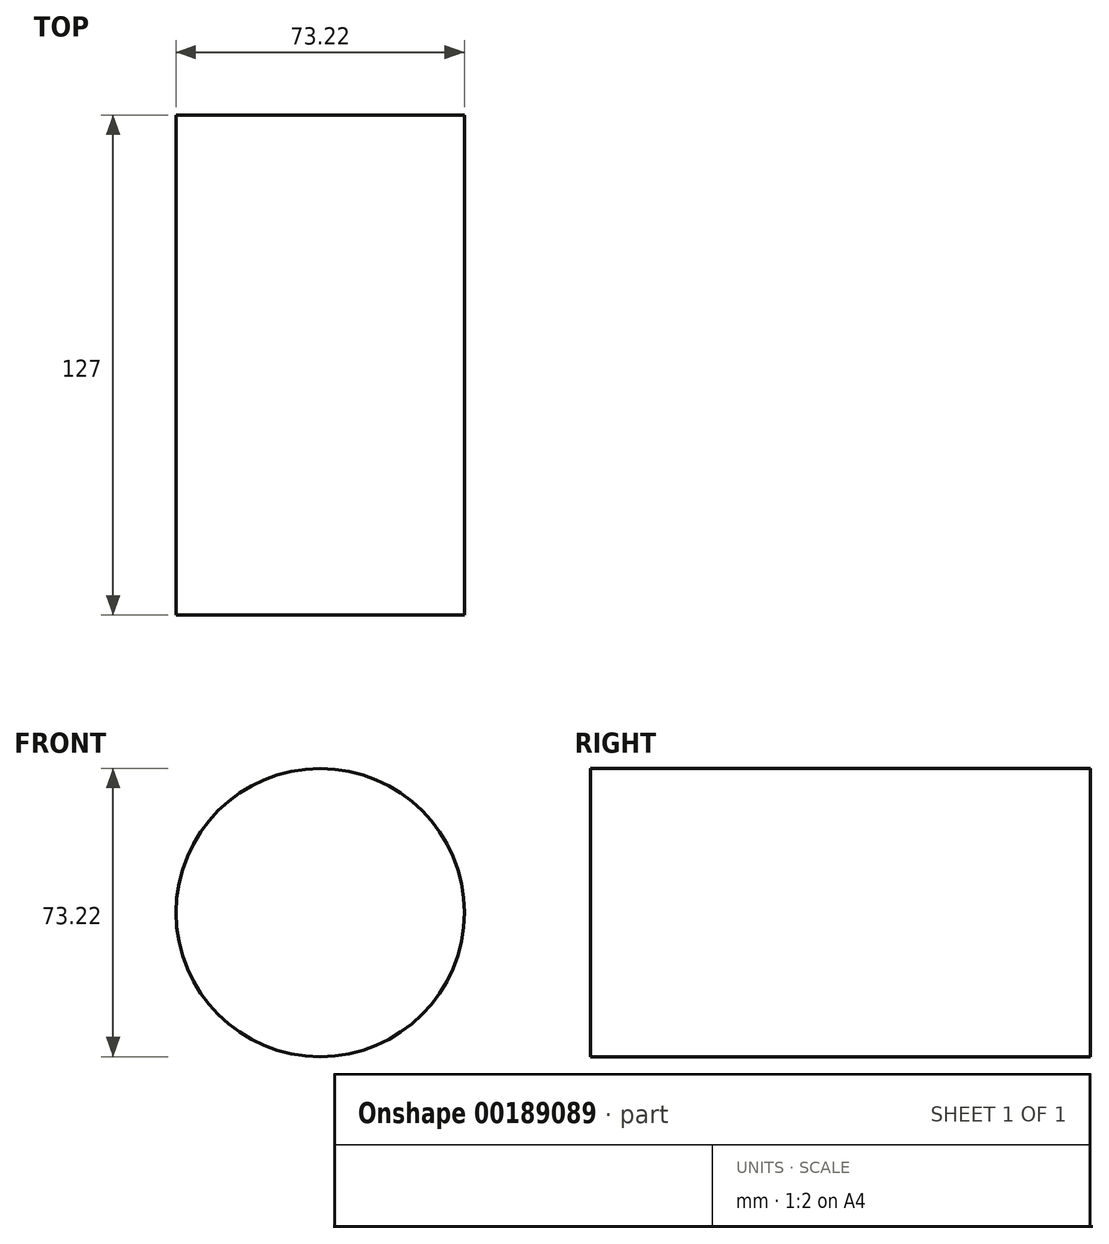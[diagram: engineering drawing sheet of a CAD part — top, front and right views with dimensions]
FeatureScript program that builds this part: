
annotation { "Feature Type Name" : "Feature", "Feature Type Description" : "" }
export const myFeature = defineFeature(function(context is Context, id is Id, definition is map)
    precondition{}
    {
        {
            var Q0;
            Q0=qCreatedBy(makeId("Front.planeOp"),FACE);
            var sketch = newSketch(context, id + "F0", { "sketchPlane" : qUnion([Q0])});
            skCircle(sketch, "E0", {"center": v(0, 0) * mm, "radius": 36.61 * mm});
            skSolve(sketch);
        }
        {
            var Q0;
            Q0=makeQuery(id+"F0.imprint","IMPRINT",FACE,{"disambiguationData":[TD([[makeQuery(id+"F0.imprint","IMPRINT",EDGE,{"derivedFrom":sQuery(id+"F0.wireOp",EDGE,"E0")}),1.0]])]});
            extrude(context, id + "F1", {"entities" : qUnion([Q0]), "depth" : 127 * mm});
        }
    });
